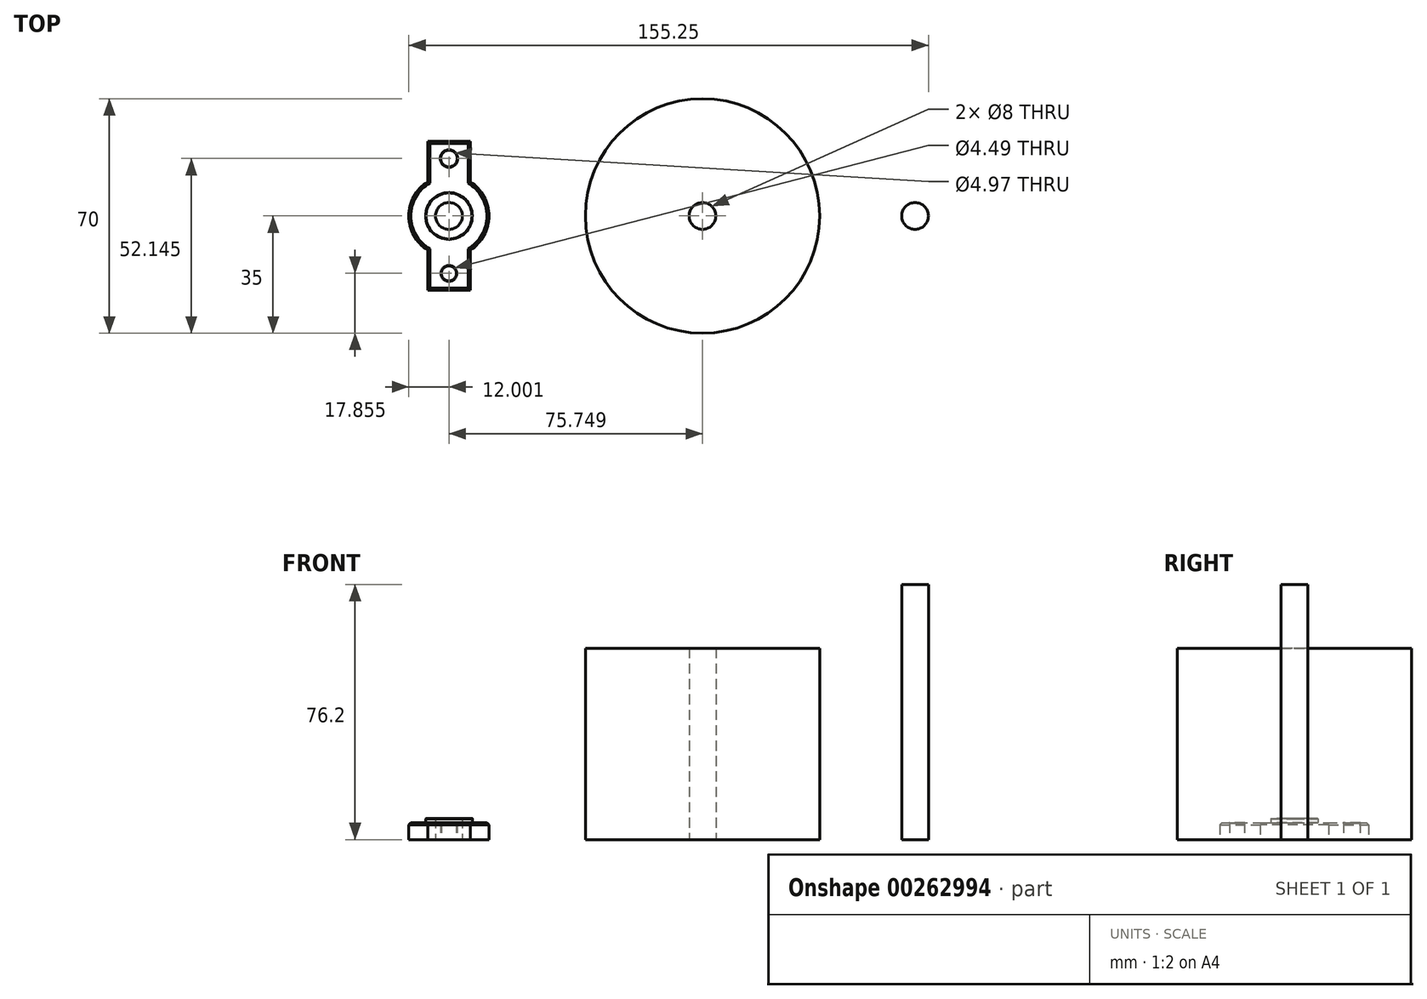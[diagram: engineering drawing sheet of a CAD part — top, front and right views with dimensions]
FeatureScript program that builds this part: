
annotation { "Feature Type Name" : "Feature", "Feature Type Description" : "" }
export const myFeature = defineFeature(function(context is Context, id is Id, definition is map)
    precondition{}
    {
        {
            var Q0;
            Q0=qCreatedBy(makeId("Top.planeOp"),FACE);
            var sketch = newSketch(context, id + "F0", { "sketchPlane" : qUnion([Q0])});
            skCircle(sketch, "E0", {"center": v(0, 0) * mm, "radius": 4 * mm});
            skCircle(sketch, "E1", {"center": v(0, 0) * mm, "radius": 35 * mm});
            skSolve(sketch);
        }
        {
            var Q0;
            Q0=makeQuery(id+"F0.imprint","IMPRINT",FACE,{"disambiguationData":[TD([[makeQuery(id+"F0.imprint","IMPRINT",EDGE,{"derivedFrom":sQuery(id+"F0.wireOp",EDGE,"E0")}),-1.0]])]});
            extrude(context, id + "F1", {"entities" : qUnion([Q0]), "depth" : 57.15 * mm});
        }
        {
            var Q0;
            Q0=qCreatedBy(makeId("Top.planeOp"),FACE);
            var sketch = newSketch(context, id + "F2", { "sketchPlane" : qUnion([Q0])});
            skCircle(sketch, "E2", {"center": v(63.5, 0) * mm, "radius": 4 * mm});
            skCircle(sketch, "E3", {"center": v(-75.75, 0) * mm, "radius": 4 * mm});
            skCircle(sketch, "E4", {"center": v(-75.75, 0) * mm, "radius": 7 * mm});
            skCircle(sketch, "E5", {"center": v(-75.75, 0) * mm, "radius": 12 * mm});
            skLineSegment(sketch, "E6.bottom", {"start": v(-69.4, -22.23) * mm, "end": v(-82.1, -22.23) * mm});
            skLineSegment(sketch, "E6.top", {"start": v(-69.4, 22.23) * mm, "end": v(-82.1, 22.23) * mm});
            skLineSegment(sketch, "E6.left", {"start": v(-69.4, -22.23) * mm, "end": v(-69.4, 22.23) * mm});
            skLineSegment(sketch, "E6.right", {"start": v(-82.1, -22.23) * mm, "end": v(-82.1, 22.23) * mm});
            skCircle(sketch, "E7", {"center": v(-75.75, 17.14) * mm, "radius": 2.49 * mm});
            skCircle(sketch, "E8", {"center": v(-75.75, -17.14) * mm, "radius": 2.24 * mm});
            skSolve(sketch);
        }
        {
            var Q0;
            {var subQ1=sQuery(id+"F2.wireOp",EDGE,"E6.top");Q0=makeQuery(id+"F2.imprint","IMPRINT",FACE,{"disambiguationData":[TD([[makeQuery(id+"F2.imprint","IMPRINT",EDGE,{"derivedFrom":subQ1}),1.0]])]});}
            var Q1;
            {var subQ1=sQuery(id+"F2.wireOp",EDGE,"E6.bottom");Q1=makeQuery(id+"F2.imprint","IMPRINT",FACE,{"disambiguationData":[TD([[makeQuery(id+"F2.imprint","IMPRINT",EDGE,{"derivedFrom":subQ1}),-1.0]])]});}
            var Q2;
            {var subQ0=sQuery(id+"F2.wireOp",EDGE,"E6.right");var subQ1=sQuery(id+"F2.wireOp",EDGE,"E4");var subQ2=makeQuery(id+"F2.imprint","INTERSECT",VERTEX,{"disambiguationData":[OD(1.0)],"derivedFrom":[subQ1,subQ0]});Q2=makeQuery(id+"F2.imprint","IMPRINT",FACE,{"disambiguationData":[TD([[makeQuery(id+"F2.imprint","IMPRINT",EDGE,{"disambiguationData":[TD([[subQ2,-1.0]])],"derivedFrom":subQ1}),-1.0]])]});}
            var Q3;
            {var subQ0=sQuery(id+"F2.wireOp",EDGE,"E6.right");var subQ1=sQuery(id+"F2.wireOp",EDGE,"E4");var subQ2=makeQuery(id+"F2.imprint","INTERSECT",VERTEX,{"disambiguationData":[OD(0.0)],"derivedFrom":[subQ1,subQ0]});Q3=makeQuery(id+"F2.imprint","IMPRINT",FACE,{"disambiguationData":[TD([[makeQuery(id+"F2.imprint","IMPRINT",EDGE,{"disambiguationData":[TD([[subQ2,1.0]])],"derivedFrom":subQ1}),-1.0]])]});}
            var Q4;
            {var subQ0=sQuery(id+"F2.wireOp",EDGE,"E6.left");var subQ1=sQuery(id+"F2.wireOp",EDGE,"E4");var subQ2=makeQuery(id+"F2.imprint","INTERSECT",VERTEX,{"disambiguationData":[OD(0.0)],"derivedFrom":[subQ1,subQ0]});Q4=makeQuery(id+"F2.imprint","IMPRINT",FACE,{"disambiguationData":[TD([[makeQuery(id+"F2.imprint","IMPRINT",EDGE,{"disambiguationData":[TD([[subQ2,1.0]])],"derivedFrom":subQ1}),-1.0]])]});}
            var Q5;
            {var subQ0=sQuery(id+"F2.wireOp",EDGE,"E6.right");var subQ1=sQuery(id+"F2.wireOp",EDGE,"E4");var subQ2=makeQuery(id+"F2.imprint","INTERSECT",VERTEX,{"disambiguationData":[OD(0.0)],"derivedFrom":[subQ1,subQ0]});Q5=makeQuery(id+"F2.imprint","IMPRINT",FACE,{"disambiguationData":[TD([[makeQuery(id+"F2.imprint","IMPRINT",EDGE,{"disambiguationData":[TD([[subQ2,-1.0]])],"derivedFrom":subQ1}),-1.0]])]});}
            extrude(context, id + "F3", {"entities" : qUnion([Q0, Q1, Q2, Q3, Q4, Q5]), "depth" : 5.08 * mm});
        }
        {
            var Q0;
            {var subQ0=sQuery(id+"F2.wireOp",EDGE,"E6.left");var subQ1=sQuery(id+"F2.wireOp",EDGE,"E4");var subQ2=makeQuery(id+"F2.imprint","INTERSECT",VERTEX,{"disambiguationData":[OD(0.0)],"derivedFrom":[subQ1,subQ0]});Q0=makeQuery(id+"F2.imprint","IMPRINT",FACE,{"disambiguationData":[TD([[makeQuery(id+"F2.imprint","IMPRINT",EDGE,{"disambiguationData":[TD([[subQ2,1.0]])],"derivedFrom":subQ1}),1.0]])]});}
            var Q1;
            Q1=makeQuery(id+"F2.imprint","IMPRINT",FACE,{"disambiguationData":[TD([[makeQuery(id+"F2.imprint","IMPRINT",EDGE,{"derivedFrom":sQuery(id+"F2.wireOp",EDGE,"E3")}),-1.0]])]});
            var Q2;
            {var subQ0=sQuery(id+"F2.wireOp",EDGE,"E6.right");var subQ1=sQuery(id+"F2.wireOp",EDGE,"E4");var subQ2=makeQuery(id+"F2.imprint","INTERSECT",VERTEX,{"disambiguationData":[OD(0.0)],"derivedFrom":[subQ1,subQ0]});Q2=makeQuery(id+"F2.imprint","IMPRINT",FACE,{"disambiguationData":[TD([[makeQuery(id+"F2.imprint","IMPRINT",EDGE,{"disambiguationData":[TD([[subQ2,-1.0]])],"derivedFrom":subQ1}),1.0]])]});}
            extrude(context, id + "F4", {"entities" : qUnion([Q0, Q1, Q2]), "operationType" : NewBodyOperationType.ADD, "depth" : 6.35 * mm});
        }
        {
            var Q0;
            {var subQ0=sQuery(id+"F2.wireOp",EDGE,"E6.right");var subQ1=sQuery(id+"F2.wireOp",EDGE,"E5");Q0=makeQuery(id+"F3.opExtrude","CAP_EDGE",EDGE,{"disambiguationData":[OSD([subQ1]),TDD([makeQuery(id+"F2.imprint","IMPRINT",EDGE,{"disambiguationData":[TD([[makeQuery(id+"F2.imprint","INTERSECT",VERTEX,{"disambiguationData":[OD(0.0)],"derivedFrom":[subQ1,subQ0]}),-1.0]])],"derivedFrom":subQ1})])],"isStart":false});}
            var Q1;
            {var subQ0=sQuery(id+"F2.wireOp",EDGE,"E6.left");Q1=makeQuery(id+"F3.opExtrude","CAP_EDGE",EDGE,{"disambiguationData":[OSD([subQ0]),TDD([makeQuery(id+"F2.imprint","IMPRINT",EDGE,{"disambiguationData":[TD([[makeQuery(id+"F2.imprint","INTERSECT",VERTEX,{"derivedFrom":[sQuery(id+"F2.wireOp",EDGE,"E6.bottom"),subQ0]}),-1.0]])],"derivedFrom":subQ0})])],"isStart":false});}
            var Q2;
            {var subQ0=sQuery(id+"F2.wireOp",EDGE,"E6.right");Q2=makeQuery(id+"F3.opExtrude","CAP_EDGE",EDGE,{"disambiguationData":[OSD([subQ0]),TDD([makeQuery(id+"F2.imprint","IMPRINT",EDGE,{"disambiguationData":[TD([[makeQuery(id+"F2.imprint","INTERSECT",VERTEX,{"derivedFrom":[sQuery(id+"F2.wireOp",EDGE,"E6.bottom"),subQ0]}),-1.0]])],"derivedFrom":subQ0})])],"isStart":false});}
            var Q3;
            Q3=makeQuery(id+"F3.opExtrude","CAP_EDGE",EDGE,{"disambiguationData":[OSD([sQuery(id+"F2.wireOp",EDGE,"E6.bottom")])],"isStart":false});
            var Q4;
            {var subQ0=sQuery(id+"F2.wireOp",EDGE,"E6.left");var subQ1=sQuery(id+"F2.wireOp",EDGE,"E5");Q4=makeQuery(id+"F3.opExtrude","CAP_EDGE",EDGE,{"disambiguationData":[OSD([subQ1]),TDD([makeQuery(id+"F2.imprint","IMPRINT",EDGE,{"disambiguationData":[TD([[makeQuery(id+"F2.imprint","INTERSECT",VERTEX,{"disambiguationData":[OD(0.0)],"derivedFrom":[subQ1,subQ0]}),1.0]])],"derivedFrom":subQ1})])],"isStart":false});}
            var Q5;
            {var subQ0=sQuery(id+"F2.wireOp",EDGE,"E6.left");Q5=makeQuery(id+"F3.opExtrude","CAP_EDGE",EDGE,{"disambiguationData":[OSD([subQ0]),TDD([makeQuery(id+"F2.imprint","IMPRINT",EDGE,{"disambiguationData":[TD([[makeQuery(id+"F2.imprint","INTERSECT",VERTEX,{"derivedFrom":[sQuery(id+"F2.wireOp",EDGE,"E6.top"),subQ0]}),1.0]])],"derivedFrom":subQ0})])],"isStart":false});}
            var Q6;
            Q6=makeQuery(id+"F3.opExtrude","CAP_EDGE",EDGE,{"disambiguationData":[OSD([sQuery(id+"F2.wireOp",EDGE,"E6.top")])],"isStart":false});
            var Q7;
            {var subQ0=sQuery(id+"F2.wireOp",EDGE,"E6.right");Q7=makeQuery(id+"F3.opExtrude","CAP_EDGE",EDGE,{"disambiguationData":[OSD([subQ0]),TDD([makeQuery(id+"F2.imprint","IMPRINT",EDGE,{"disambiguationData":[TD([[makeQuery(id+"F2.imprint","INTERSECT",VERTEX,{"derivedFrom":[sQuery(id+"F2.wireOp",EDGE,"E6.top"),subQ0]}),1.0]])],"derivedFrom":subQ0})])],"isStart":false});}
            chamfer(context, id + "F5", {"entities" : qUnion([Q0, Q1, Q2, Q3, Q4, Q5, Q6, Q7]), "width" : 0.64 * mm, "tangentPropagation" : true});
        }
        {
            var Q0;
            Q0=makeQuery(id+"F3.opExtrude","CAP_EDGE",EDGE,{"disambiguationData":[OSD([sQuery(id+"F2.wireOp",EDGE,"E7")])],"isStart":false});
            var Q1;
            Q1=makeQuery(id+"F3.opExtrude","CAP_EDGE",EDGE,{"disambiguationData":[OSD([sQuery(id+"F2.wireOp",EDGE,"E8")])],"isStart":false});
            var Q2;
            Q2=makeQuery(id+"F4.opExtrude","CAP_EDGE",EDGE,{"disambiguationData":[OSD([sQuery(id+"F2.wireOp",EDGE,"E4")])],"isStart":false});
            chamfer(context, id + "F6", {"entities" : qUnion([Q0, Q1, Q2]), "width" : 0.13 * mm, "tangentPropagation" : true});
        }
        {
            var Q0;
            Q0=makeQuery(id+"F2.imprint","IMPRINT",FACE,{"disambiguationData":[TD([[makeQuery(id+"F2.imprint","IMPRINT",EDGE,{"derivedFrom":sQuery(id+"F2.wireOp",EDGE,"E2")}),1.0]])]});
            extrude(context, id + "F7", {"entities" : qUnion([Q0]), "depth" : 76.2 * mm});
        }
    });
